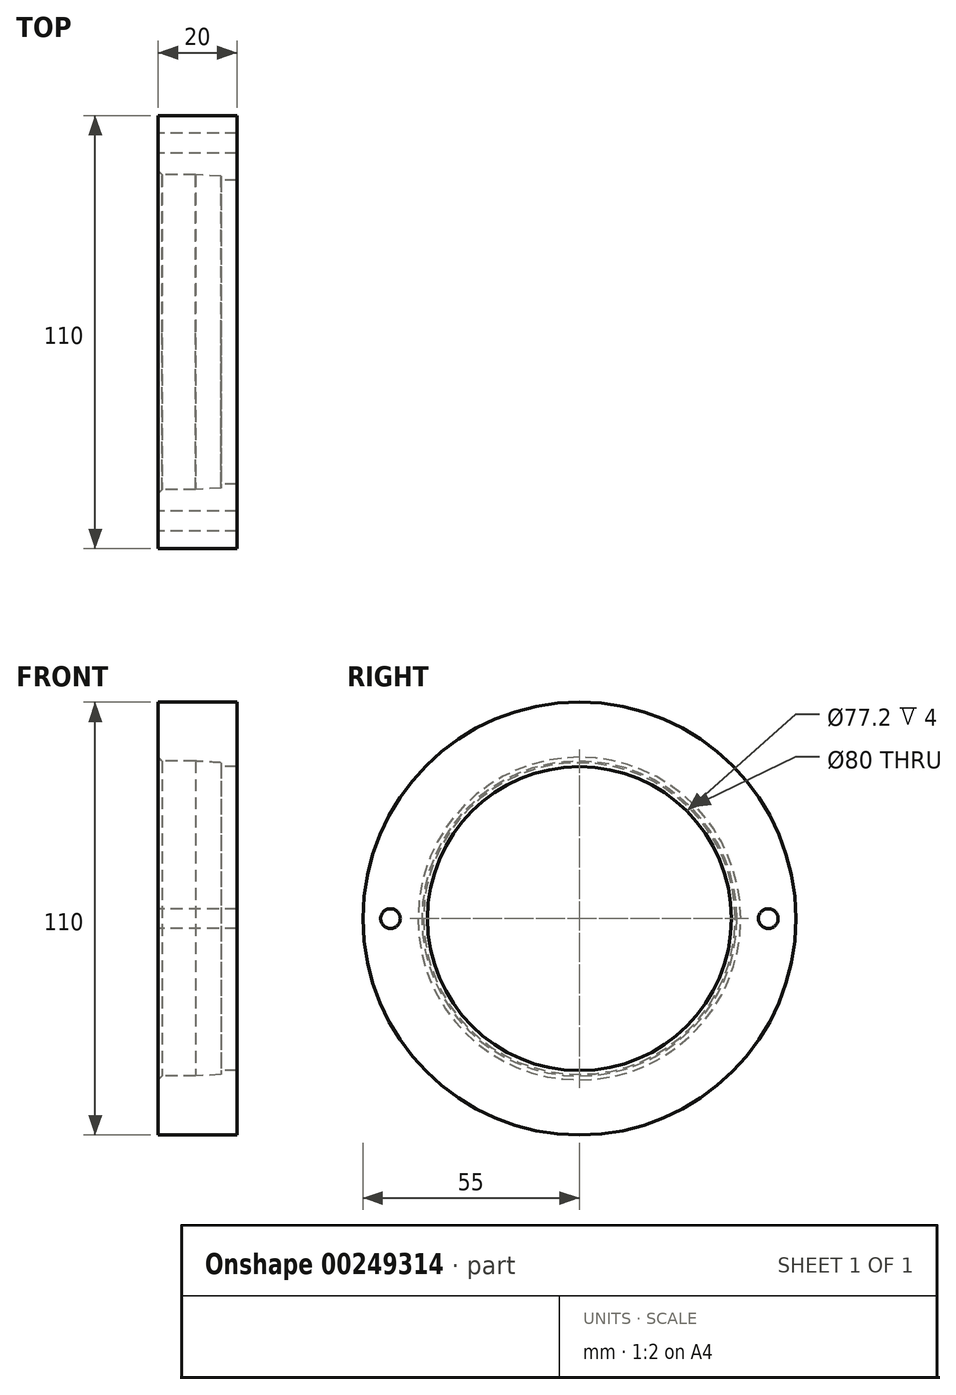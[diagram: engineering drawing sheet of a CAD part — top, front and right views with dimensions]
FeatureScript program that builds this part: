
annotation { "Feature Type Name" : "Feature", "Feature Type Description" : "" }
export const myFeature = defineFeature(function(context is Context, id is Id, definition is map)
    precondition{}
    {
        {
            var Q0;
            Q0=qCreatedBy(makeId("Front.planeOp"),FACE);
            var sketch = newSketch(context, id + "F0", { "sketchPlane" : qUnion([Q0])});
            skLineSegment(sketch, "E0", {"start": v(0, 38.6) * mm, "end": v(0, 55) * mm});
            skLineSegment(sketch, "E1", {"start": v(0, 55) * mm, "end": v(-20, 55) * mm});
            skLineSegment(sketch, "E2", {"start": v(-4, 38.6) * mm, "end": v(-4, 39.6) * mm});
            skLineSegment(sketch, "E3", {"start": v(-10.54, 40) * mm, "end": v(-20, 40) * mm});
            skLineSegment(sketch, "E4", {"start": v(0, 0) * mm, "end": v(24.78, 0) * mm});
            skLineSegment(sketch, "E5", {"start": v(-4, 38.6) * mm, "end": v(0, 38.6) * mm});
            skLineSegment(sketch, "E6", {"start": v(-20, 40) * mm, "end": v(-20, 55) * mm});
            skLineSegment(sketch, "E7", {"start": v(-4, 39.6) * mm, "end": v(-10.54, 40) * mm});
            skSolve(sketch);
        }
        {
            var Q0;
            Q0=makeQuery(id+"F0.imprint","IMPRINT",FACE,{"disambiguationData":[TD([[makeQuery(id+"F0.imprint","IMPRINT",EDGE,{"derivedFrom":sQuery(id+"F0.wireOp",EDGE,"E0")}),1.0]])]});
            var Q1;
            Q1=sQuery(id+"F0.wireOp",EDGE,"E4");
            revolve(context, id + "F1", {"entities" : qUnion([Q0]), "axis" : qUnion([Q1]), "revolveType" : RevolveType.FULL});
        }
        {
            var Q0;
            Q0=makeQuery(id+"F1.opRevolve","SWEPT_EDGE",EDGE,{"disambiguationData":[OSD([sQuery(id+"F0.wireOp",EDGE,"E3"),sQuery(id+"F0.wireOp",EDGE,"E6")])]});
            chamfer(context, id + "F2", {"entities" : qUnion([Q0]), "width" : 1 * mm, "tangentPropagation" : true});
        }
        {
            var Q0;
            Q0=makeQuery(id+"F1.opRevolve","SWEPT_FACE",FACE,{"disambiguationData":[OSD([sQuery(id+"F0.wireOp",EDGE,"E6")])]});
            var sketch = newSketch(context, id + "F3", { "sketchPlane" : qUnion([Q0])});
            skCircle(sketch, "E8", {"center": v(48, 0) * mm, "radius": 2.5 * mm});
            skSolve(sketch);
        }
        {
            var Q0;
            Q0=makeQuery(id+"F3.imprint","IMPRINT",FACE,{"disambiguationData":[TD([[makeQuery(id+"F3.imprint","IMPRINT",EDGE,{"derivedFrom":sQuery(id+"F3.wireOp",EDGE,"E8")}),1.0]])]});
            extrude(context, id + "F4", {"entities" : qUnion([Q0]), "operationType" : NewBodyOperationType.REMOVE, "endBound" : BoundingType.THROUGH_ALL, "oppositeDirection" : true, "depth" : 25 * mm, "offsetDistance" : 25 * mm});
        }
        {
            var Q0;
            Q0=makeQuery(id+"F1.opRevolve","SWEPT_FACE",FACE,{"disambiguationData":[OSD([sQuery(id+"F0.wireOp",EDGE,"E6")])]});
            var sketch = newSketch(context, id + "F5", { "sketchPlane" : qUnion([Q0])});
            skCircle(sketch, "E9", {"center": v(-48, 0) * mm, "radius": 2.5 * mm});
            skSolve(sketch);
        }
        {
            var Q0;
            Q0=makeQuery(id+"F5.imprint","IMPRINT",FACE,{"disambiguationData":[TD([[makeQuery(id+"F5.imprint","IMPRINT",EDGE,{"derivedFrom":sQuery(id+"F5.wireOp",EDGE,"E9")}),1.0]])]});
            extrude(context, id + "F6", {"entities" : qUnion([Q0]), "operationType" : NewBodyOperationType.REMOVE, "endBound" : BoundingType.THROUGH_ALL, "oppositeDirection" : true, "depth" : 25 * mm, "offsetDistance" : 25 * mm});
        }
    });
